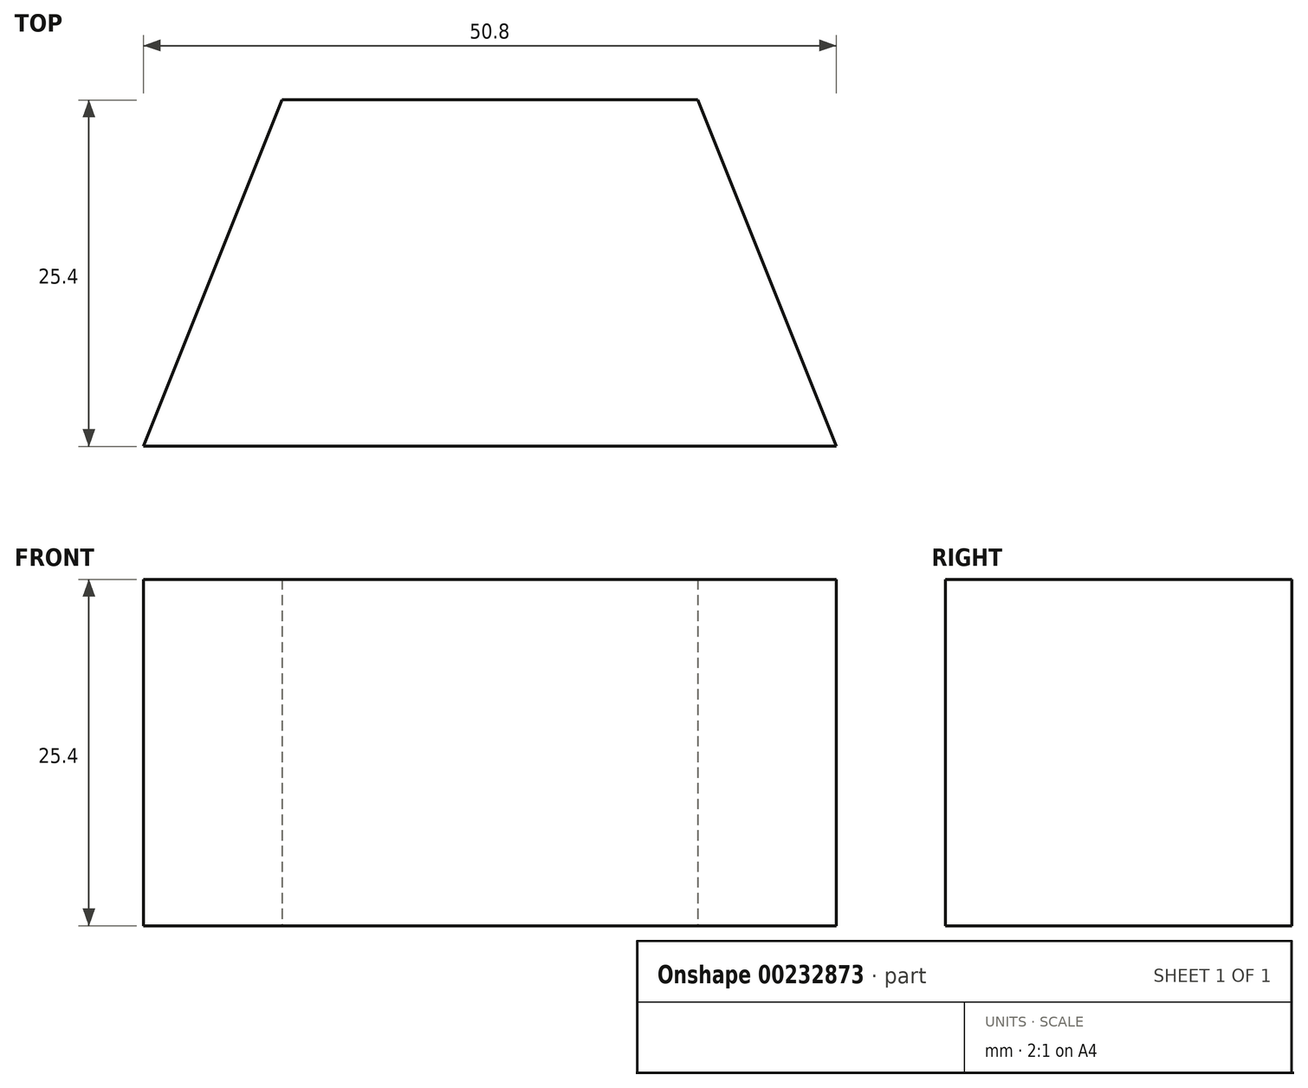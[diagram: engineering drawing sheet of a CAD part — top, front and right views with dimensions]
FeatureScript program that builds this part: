
annotation { "Feature Type Name" : "Feature", "Feature Type Description" : "" }
export const myFeature = defineFeature(function(context is Context, id is Id, definition is map)
    precondition{}
    {
        {
            var Q0;
            Q0=qCreatedBy(makeId("Top.planeOp"),FACE);
            var sketch = newSketch(context, id + "F0", { "sketchPlane" : qUnion([Q0])});
            skLineSegment(sketch, "E0", {"start": v(-24.2, -56.96) * mm, "end": v(26.6, -56.96) * mm});
            skLineSegment(sketch, "E1", {"start": v(16.43, -31.56) * mm, "end": v(-14.05, -31.56) * mm});
            skLineSegment(sketch, "E2", {"start": v(-14.05, -31.56) * mm, "end": v(16.43, -31.56) * mm});
            skLineSegment(sketch, "E3", {"start": v(-24.2, -56.96) * mm, "end": v(-14.05, -31.56) * mm});
            skLineSegment(sketch, "E4", {"start": v(26.6, -56.96) * mm, "end": v(16.43, -31.56) * mm});
            skSolve(sketch);
        }
        {
            var Q0;
            Q0=makeQuery(id+"F0.imprint","IMPRINT",FACE,{"disambiguationData":[TD([[makeQuery(id+"F0.imprint","IMPRINT",EDGE,{"derivedFrom":sQuery(id+"F0.wireOp",EDGE,"E0")}),1.0]])]});
            extrude(context, id + "F1", {"entities" : qUnion([Q0]), "depth" : 25.4 * mm});
        }
    });
